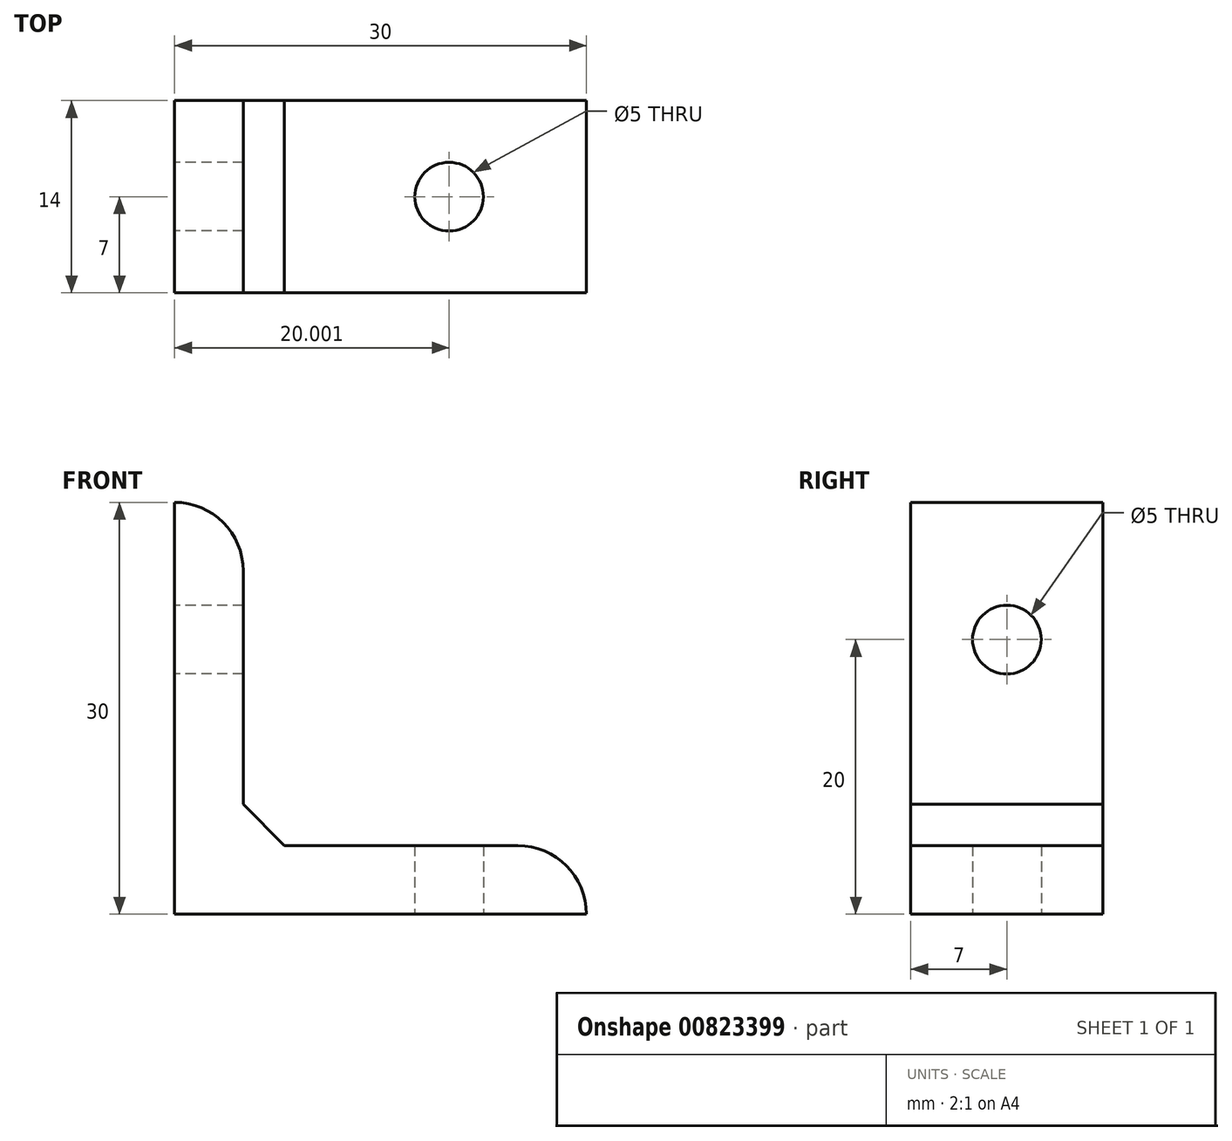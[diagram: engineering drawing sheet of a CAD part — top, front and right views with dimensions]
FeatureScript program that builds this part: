
annotation { "Feature Type Name" : "Feature", "Feature Type Description" : "" }
export const myFeature = defineFeature(function(context is Context, id is Id, definition is map)
    precondition{}
    {
        {
            var Q0;
            Q0=qCreatedBy(makeId("Front.planeOp"),FACE);
            var sketch = newSketch(context, id + "F0", { "sketchPlane" : qUnion([Q0])});
            skLineSegment(sketch, "E0", {"start": v(-11.29, 17.02) * mm, "end": v(-11.29, -12.98) * mm});
            skLineSegment(sketch, "E1", {"start": v(-11.29, -12.98) * mm, "end": v(18.71, -12.98) * mm});
            skArc(sketch, "E2", {"start": v(-6.29, 12.02) * mm, "mid": v(-7.75, 15.56) * mm, "end": v(-11.29, 17.02) * mm});
            skLineSegment(sketch, "E3", {"start": v(-6.29, 12.02) * mm, "end": v(-6.29, -4.98) * mm});
            skLineSegment(sketch, "E4", {"start": v(-3.29, -7.98) * mm, "end": v(-6.29, -4.98) * mm});
            skLineSegment(sketch, "E5", {"start": v(-11.84, 7.02) * mm, "end": v(-5.72, 7.02) * mm});
            skLineSegment(sketch, "E6", {"start": v(8.71, -13.53) * mm, "end": v(8.71, -7.4) * mm});
            skLineSegment(sketch, "E7", {"start": v(13.71, -7.98) * mm, "end": v(-3.29, -7.98) * mm});
            skArc(sketch, "E8", {"start": v(18.71, -12.98) * mm, "mid": v(17.25, -9.44) * mm, "end": v(13.71, -7.98) * mm});
            skSolve(sketch);
        }
        {
            var Q0;
            {var subQ0=sQuery(id+"F0.wireOp",EDGE,"E4");Q0=makeQuery(id+"F0.imprint","IMPRINT",FACE,{"disambiguationData":[TD([[makeQuery(id+"F0.imprint","IMPRINT",EDGE,{"derivedFrom":subQ0}),1.0]])]});}
            var Q1;
            {var subQ0=sQuery(id+"F0.wireOp",EDGE,"E8");Q1=makeQuery(id+"F0.imprint","IMPRINT",FACE,{"disambiguationData":[TD([[makeQuery(id+"F0.imprint","IMPRINT",EDGE,{"derivedFrom":subQ0}),1.0]])]});}
            var Q2;
            {var subQ0=sQuery(id+"F0.wireOp",EDGE,"E2");Q2=makeQuery(id+"F0.imprint","IMPRINT",FACE,{"disambiguationData":[TD([[makeQuery(id+"F0.imprint","IMPRINT",EDGE,{"derivedFrom":subQ0}),1.0]])]});}
            extrude(context, id + "F1", {"entities" : qUnion([Q0, Q1, Q2]), "oppositeDirection" : true, "depth" : 14 * mm, "offsetDistance" : 25 * mm});
        }
        {
            var Q0;
            Q0=makeQuery(id+"F1.opExtrude","SWEPT_FACE",FACE,{"disambiguationData":[OSD([sQuery(id+"F0.wireOp",EDGE,"E0")])]});
            var sketch = newSketch(context, id + "F2", { "sketchPlane" : qUnion([Q0])});
            skLineSegment(sketch, "E9", {"start": v(-14, 17.02) * mm, "end": v(0, 17.02) * mm});
            skLineSegment(sketch, "E10", {"start": v(0, 17.02) * mm, "end": v(0, 0) * mm});
            skCircle(sketch, "E11", {"center": v(-7, 7.02) * mm, "radius": 2.5 * mm});
            skSolve(sketch);
        }
        {
            var Q0;
            Q0=makeQuery(id+"F2.imprint","IMPRINT",FACE,{"disambiguationData":[TD([[makeQuery(id+"F2.imprint","IMPRINT",EDGE,{"derivedFrom":sQuery(id+"F2.wireOp",EDGE,"E11")}),1.0]])]});
            extrude(context, id + "F3", {"entities" : qUnion([Q0]), "operationType" : NewBodyOperationType.REMOVE, "oppositeDirection" : true, "depth" : 5 * mm, "offsetDistance" : 25 * mm});
        }
        {
            var Q0;
            Q0=makeQuery(id+"F1.opExtrude","SWEPT_FACE",FACE,{"disambiguationData":[OSD([sQuery(id+"F0.wireOp",EDGE,"E1")])]});
            var sketch = newSketch(context, id + "F4", { "sketchPlane" : qUnion([Q0])});
            skCircle(sketch, "E12", {"center": v(8.71, -7) * mm, "radius": 2.5 * mm});
            skSolve(sketch);
        }
        {
            var Q0;
            Q0 = qSketchRegion(id + "F4", true);
            extrude(context, id + "F5", {"entities" : qUnion([Q0]), "operationType" : NewBodyOperationType.REMOVE, "oppositeDirection" : true, "depth" : 5 * mm, "offsetDistance" : 25 * mm});
        }
    });
